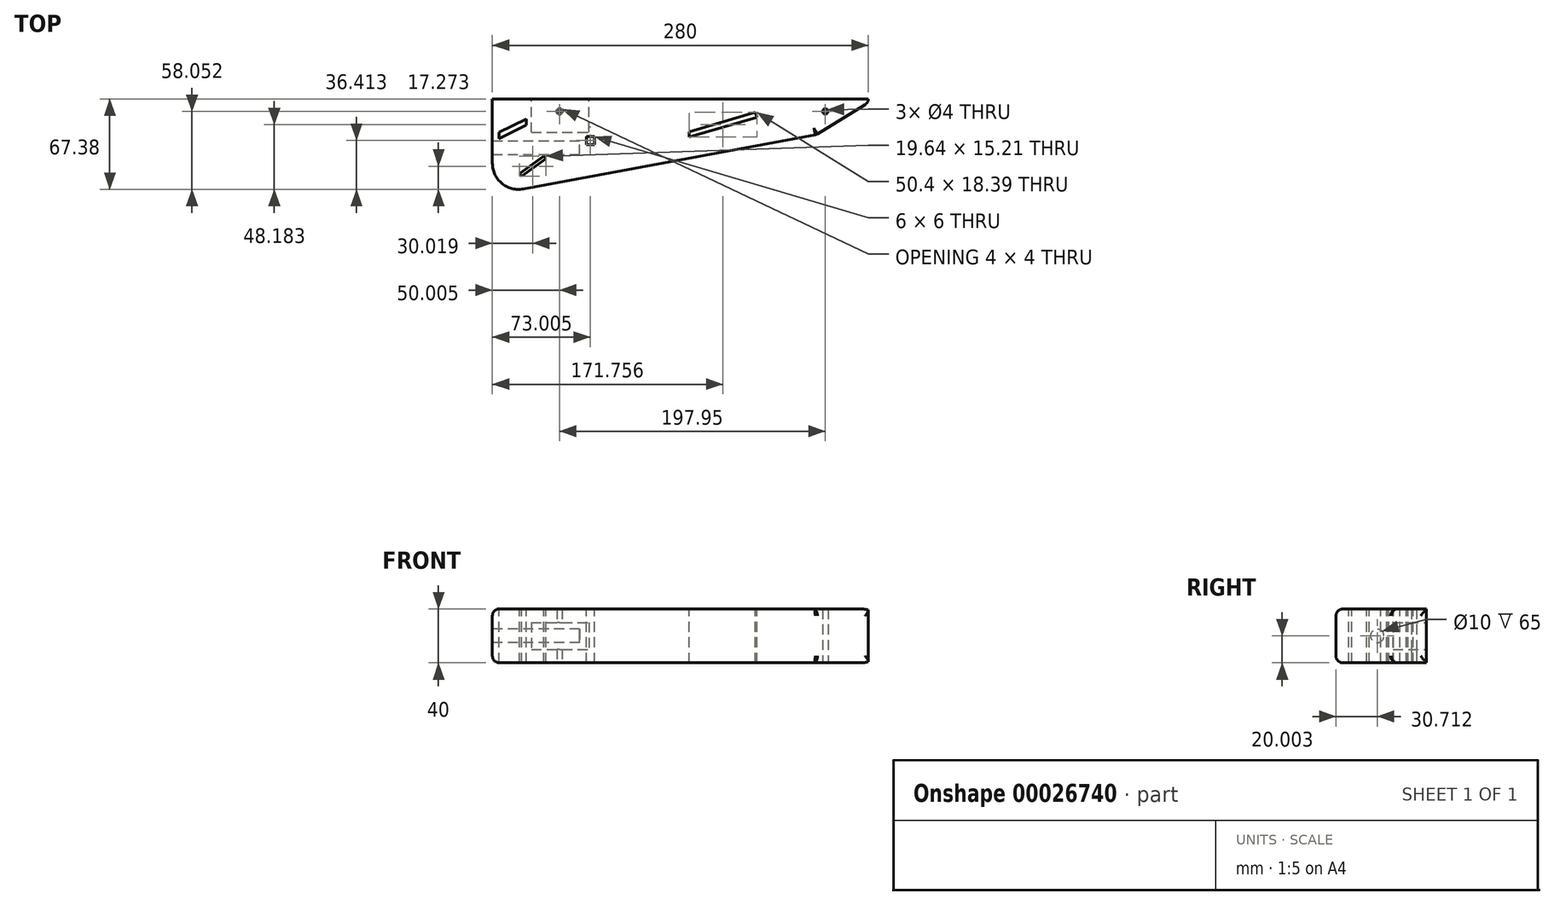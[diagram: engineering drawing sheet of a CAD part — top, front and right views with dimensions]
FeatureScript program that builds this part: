
annotation { "Feature Type Name" : "Feature", "Feature Type Description" : "" }
export const myFeature = defineFeature(function(context is Context, id is Id, definition is map)
    precondition{}
    {
        {
            var Q0;
            Q0=qCreatedBy(makeId("Front.planeOp"),FACE);
            var sketch = newSketch(context, id + "F0", { "sketchPlane" : qUnion([Q0])});
            skLineSegment(sketch, "E0.bottom", {"start": v(-73.62, -33.97) * mm, "end": v(206.38, -33.97) * mm});
            skLineSegment(sketch, "E0.top", {"start": v(-73.62, 37.36) * mm, "end": v(206.38, 37.36) * mm});
            skLineSegment(sketch, "E0.left", {"start": v(-73.62, -33.97) * mm, "end": v(-73.62, 13.94) * mm});
            skLineSegment(sketch, "E0.right", {"start": v(206.38, -33.97) * mm, "end": v(206.38, -31.3) * mm});
            skLineSegment(sketch, "E1", {"start": v(-50.6, 33.08) * mm, "end": v(190.04, -11.63) * mm});
            skPoint(sketch, "E2.newPointB", {"position": v(206.38, 36.03) * mm});
            skArc(sketch, "E2.filletArc", {"start": v(206.38, -31.3) * mm, "mid": v(201.76, -18.5) * mm, "end": v(190.04, -11.63) * mm});
            skPoint(sketch, "E3.visualSharp", {"position": v(-73.62, 37.36) * mm});
            skArc(sketch, "E3.filletArc", {"start": v(-50.6, 33.08) * mm, "mid": v(-66.6, 28.91) * mm, "end": v(-73.62, 13.94) * mm});
            skLineSegment(sketch, "E4.bottom", {"start": v(2.38, 0) * mm, "end": v(-3.62, 0) * mm});
            skLineSegment(sketch, "E4.top", {"start": v(2.38, -6) * mm, "end": v(-3.62, -6) * mm});
            skLineSegment(sketch, "E4.left", {"start": v(2.38, 0) * mm, "end": v(2.38, -6) * mm});
            skLineSegment(sketch, "E4.right", {"start": v(-3.62, 0) * mm, "end": v(-3.62, -6) * mm});
            skLineSegment(sketch, "E5", {"start": v(-68.62, -9.03) * mm, "end": v(-48.43, -18.97) * mm});
            skLineSegment(sketch, "E6", {"start": v(-48.43, -18.97) * mm, "end": v(-48.43, -14.36) * mm});
            skLineSegment(sketch, "E7", {"start": v(-48.43, -14.36) * mm, "end": v(-68.62, -4.42) * mm});
            skLineSegment(sketch, "E8", {"start": v(-68.62, -4.42) * mm, "end": v(-68.62, -9.03) * mm});
            skLineSegment(sketch, "E9", {"start": v(-53.42, 21.8) * mm, "end": v(-35.25, 8.53) * mm});
            skLineSegment(sketch, "E10", {"start": v(-35.25, 8.53) * mm, "end": v(-33.78, 10.55) * mm});
            skLineSegment(sketch, "E11", {"start": v(-33.78, 10.55) * mm, "end": v(-51.85, 23.75) * mm});
            skLineSegment(sketch, "E12", {"start": v(-51.85, 23.75) * mm, "end": v(-53.42, 21.8) * mm});
            skLineSegment(sketch, "E13", {"start": v(72.94, -5.57) * mm, "end": v(123.33, -20.28) * mm});
            skLineSegment(sketch, "E14", {"start": v(123.33, -20.28) * mm, "end": v(122.26, -23.97) * mm});
            skLineSegment(sketch, "E15", {"start": v(122.26, -23.97) * mm, "end": v(72.94, -9.57) * mm});
            skLineSegment(sketch, "E16", {"start": v(72.94, -9.57) * mm, "end": v(72.94, -5.57) * mm});
            skLineSegment(sketch, "E17", {"start": v(206.38, -31.3) * mm, "end": v(167.69, -7.48) * mm});
            skSolve(sketch);
        }
        {
            var Q0;
            Q0=makeQuery(id+"F0.imprint","IMPRINT",FACE,{"disambiguationData":[TD([[makeQuery(id+"F0.imprint","IMPRINT",EDGE,{"derivedFrom":sQuery(id+"F0.wireOp",EDGE,"E0.bottom")}),1.0]])]});
            extrude(context, id + "F1", {"entities" : qUnion([Q0]), "depth" : 40 * mm});
        }
        {
            var Q0;
            Q0=makeQuery(id+"F1.opExtrude","SWEPT_FACE",FACE,{"disambiguationData":[OSD([sQuery(id+"F0.wireOp",EDGE,"E0.left")])]});
            var sketch = newSketch(context, id + "F2", { "sketchPlane" : qUnion([Q0])});
            skCircle(sketch, "E18", {"center": v(20, 2.7) * mm, "radius": 5 * mm});
            skSolve(sketch);
        }
        {
            var Q0;
            Q0=makeQuery(id+"F2.imprint","IMPRINT",FACE,{"disambiguationData":[TD([[makeQuery(id+"F2.imprint","IMPRINT",EDGE,{"derivedFrom":sQuery(id+"F2.wireOp",EDGE,"E18")}),1.0]])]});
            extrude(context, id + "F3", {"entities" : qUnion([Q0]), "operationType" : NewBodyOperationType.REMOVE, "oppositeDirection" : true, "depth" : 65 * mm});
        }
        {
            var Q0;
            Q0=makeQuery(id+"F1.opExtrude","CAP_FACE",FACE,{"disambiguationData":[OSD([sQuery(id+"F0.wireOp",EDGE,"E0.bottom"),sQuery(id+"F0.wireOp",EDGE,"E0.top"),sQuery(id+"F0.wireOp",EDGE,"E0.left"),sQuery(id+"F0.wireOp",EDGE,"E0.right")])],"isStart":false});
            var sketch = newSketch(context, id + "F4", { "sketchPlane" : qUnion([Q0])});
            skCircle(sketch, "E19", {"center": v(-23.62, -24.64) * mm, "radius": 2 * mm});
            skCircle(sketch, "E20", {"center": v(174.33, -24.64) * mm, "radius": 2 * mm});
            skSolve(sketch);
        }
        {
            var Q0;
            Q0=makeQuery(id+"F4.imprint","IMPRINT",FACE,{"disambiguationData":[TD([[makeQuery(id+"F4.imprint","IMPRINT",EDGE,{"derivedFrom":sQuery(id+"F4.wireOp",EDGE,"E19")}),1.0]])]});
            var Q1;
            Q1=makeQuery(id+"F4.imprint","IMPRINT",FACE,{"disambiguationData":[TD([[makeQuery(id+"F4.imprint","IMPRINT",EDGE,{"derivedFrom":sQuery(id+"F4.wireOp",EDGE,"E20")}),1.0]])]});
            extrude(context, id + "F5", {"entities" : qUnion([Q0, Q1]), "operationType" : NewBodyOperationType.REMOVE, "endBound" : BoundingType.THROUGH_ALL, "oppositeDirection" : true, "depth" : 25 * mm});
        }
        {
            var Q0;
            Q0=makeQuery(id+"F1.opExtrude","SWEPT_FACE",FACE,{"disambiguationData":[OSD([sQuery(id+"F0.wireOp",EDGE,"E0.bottom")])]});
            var sketch = newSketch(context, id + "F6", { "sketchPlane" : qUnion([Q0])});
            skLineSegment(sketch, "E21.bottom", {"start": v(-44.62, 10) * mm, "end": v(-1.62, 10) * mm});
            skLineSegment(sketch, "E21.top", {"start": v(-44.62, 30) * mm, "end": v(-1.62, 30) * mm});
            skLineSegment(sketch, "E21.left", {"start": v(-44.62, 10) * mm, "end": v(-44.62, 30) * mm});
            skLineSegment(sketch, "E21.right", {"start": v(-1.62, 10) * mm, "end": v(-1.62, 30) * mm});
            skSolve(sketch);
        }
        {
            var Q0;
            Q0=makeQuery(id+"F6.imprint","IMPRINT",FACE,{"disambiguationData":[TD([[makeQuery(id+"F6.imprint","IMPRINT",EDGE,{"derivedFrom":sQuery(id+"F6.wireOp",EDGE,"E21.bottom")}),1.0]])]});
            extrude(context, id + "F7", {"entities" : qUnion([Q0]), "operationType" : NewBodyOperationType.REMOVE, "oppositeDirection" : true, "depth" : 25 * mm});
        }
        {
            var Q0;
            Q0=makeQuery(id+"F1.opExtrude","SWEPT_FACE",FACE,{"disambiguationData":[OSD([sQuery(id+"F0.wireOp",EDGE,"E1")])]});
            fillet(context, id + "F8", {"entities" : qUnion([Q0]), "radius" : 5 * mm, "tangentPropagation" : true, "allowEdgeOverflow" : false});
        }
        {
            var Q0;
            Q0=makeQuery(id+"F1.opExtrude","CAP_EDGE",EDGE,{"disambiguationData":[OSD([sQuery(id+"F0.wireOp",EDGE,"E17")])],"isStart":true});
            var Q1;
            Q1=makeQuery(id+"F1.opExtrude","SWEPT_EDGE",EDGE,{"disambiguationData":[OSD([sQuery(id+"F0.wireOp",EDGE,"E0.right"),sQuery(id+"F0.wireOp",EDGE,"E2.filletArc"),sQuery(id+"F0.wireOp",EDGE,"E17")])]});
            var Q2;
            Q2=makeQuery(id+"F1.opExtrude","CAP_EDGE",EDGE,{"disambiguationData":[OSD([sQuery(id+"F0.wireOp",EDGE,"E17")])],"isStart":false});
            fillet(context, id + "F9", {"entities" : qUnion([Q0, Q1, Q2]), "radius" : 5 * mm, "tangentPropagation" : true, "allowEdgeOverflow" : false});
        }
        {
            var Q0;
            Q0=makeQuery(id+"F1.opExtrude","SWEPT_BODY",BODY,{"disambiguationData":[OSD([sQuery(id+"F0.wireOp",EDGE,"E0.bottom"),sQuery(id+"F0.wireOp",EDGE,"E0.left"),sQuery(id+"F0.wireOp",EDGE,"E0.right"),sQuery(id+"F0.wireOp",EDGE,"E1"),sQuery(id+"F0.wireOp",EDGE,"E3.filletArc"),sQuery(id+"F0.wireOp",EDGE,"E4.bottom"),sQuery(id+"F0.wireOp",EDGE,"E4.top"),sQuery(id+"F0.wireOp",EDGE,"E4.left"),sQuery(id+"F0.wireOp",EDGE,"E4.right"),sQuery(id+"F0.wireOp",EDGE,"E5"),sQuery(id+"F0.wireOp",EDGE,"E6"),sQuery(id+"F0.wireOp",EDGE,"E7"),sQuery(id+"F0.wireOp",EDGE,"E8"),sQuery(id+"F0.wireOp",EDGE,"E9"),sQuery(id+"F0.wireOp",EDGE,"E10"),sQuery(id+"F0.wireOp",EDGE,"E11"),sQuery(id+"F0.wireOp",EDGE,"E12"),sQuery(id+"F0.wireOp",EDGE,"E13"),sQuery(id+"F0.wireOp",EDGE,"E14"),sQuery(id+"F0.wireOp",EDGE,"E15"),sQuery(id+"F0.wireOp",EDGE,"E16"),sQuery(id+"F0.wireOp",EDGE,"E17")])]});
            var Q1;
            Q1=makeQuery(id+"F1.opExtrude","CAP_EDGE",EDGE,{"disambiguationData":[OSD([sQuery(id+"F0.wireOp",EDGE,"E0.bottom")])],"isStart":false});
            transform(context, id + "F10", {"entities" : qUnion([Q0]), "transformType" : TransformType.ROTATION, "transformAxis" : qUnion([Q1]), "angle" : 90 * degree, "makeCopy" : false});
        }
    });
